# Revit family: Haworth_LC15_Table
name_source: partatom
category: Furniture
revit_build: Autodesk Revit 2018 (Build: 20170223_1515(x64)
units: mm (PartAtom-declared; Revit-internal decimal feet)

## family parameters
Always vertical = Yes
Cut with Voids When Loaded = No
OmniClass Number = 23.40.70.14.64.21
OmniClass Title = Systems Furniture
Room Calculation Point = No
Shared = No
Work Plane-Based = No

## types (1)
- HCCS-L15T - Round
    Actual Depth = 72 3/4"
    Actual Height = 27 125/128"
    Actual Width = 72 3/4"
    Assembly Code = E2020200
    Description = Haworth LC15 Table
    Frame Height = 1 5/16"
    Frame Offset = 3/16"
    Glide Height = 5/16"
    Leg Half = 1"
    Manufacturer = Haworth
    Model = HCCS-L15T
    Revision Number = 1
    Size = Verify Final Dim. w/ Haworth
    Support Location Offset = 3/8"
    Support Location_Front_Back = 20"
    Support Location_Side = 20"
    Table Top Thickness = 1 145/256"
    URL = http://www.haworth.com
    URL - Product = http://www.haworth.com
    Warranty = http://www.haworth.com

## geometry (parser evidence)
native form markers: Sweep x2
no freeform markers — native parametric forms only
